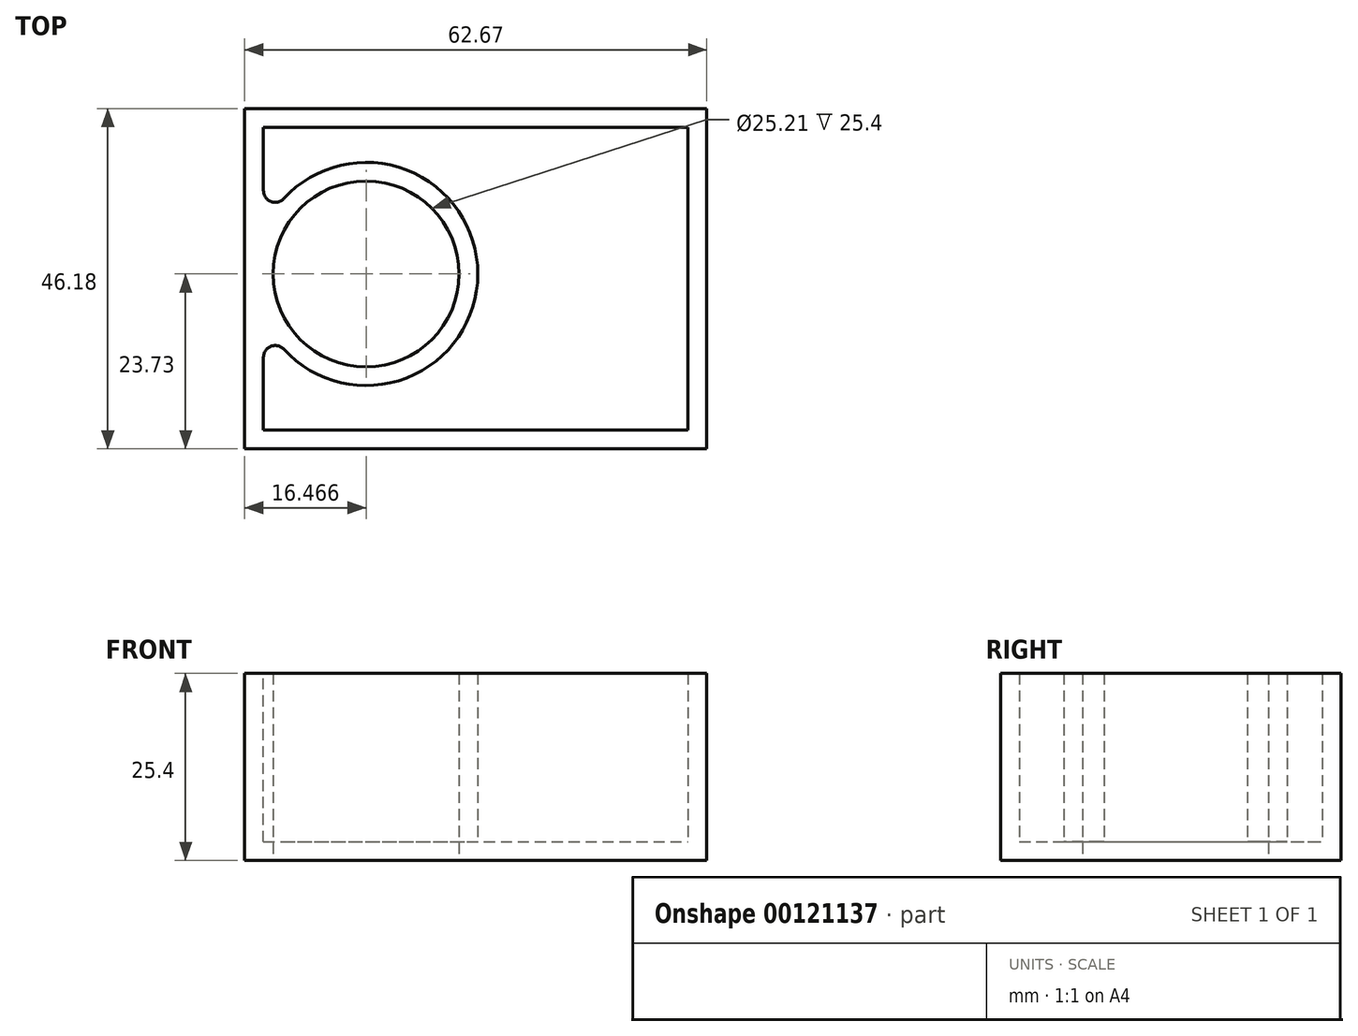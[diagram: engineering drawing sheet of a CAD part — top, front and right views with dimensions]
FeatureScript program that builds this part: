
annotation { "Feature Type Name" : "Feature", "Feature Type Description" : "" }
export const myFeature = defineFeature(function(context is Context, id is Id, definition is map)
    precondition{}
    {
        {
            var Q0;
            Q0=qCreatedBy(makeId("Top.planeOp"),FACE);
            var sketch = newSketch(context, id + "F0", { "sketchPlane" : qUnion([Q0])});
            skLineSegment(sketch, "E0.bottom", {"start": v(0, 0) * mm, "end": v(62.67, 0) * mm});
            skLineSegment(sketch, "E0.top", {"start": v(0, 46.18) * mm, "end": v(62.67, 46.18) * mm});
            skLineSegment(sketch, "E0.left", {"start": v(0, 0) * mm, "end": v(0, 46.18) * mm});
            skLineSegment(sketch, "E0.right", {"start": v(62.67, 0) * mm, "end": v(62.67, 46.18) * mm});
            skCircle(sketch, "E1", {"center": v(16.47, 23.73) * mm, "radius": 12.6 * mm});
            skSolve(sketch);
        }
        {
            var Q0;
            Q0 = qSketchRegion(id + "F0", true);
            extrude(context, id + "F1", {"entities" : qUnion([Q0]), "depth" : 25.4 * mm});
        }
        {
            var Q0;
            Q0=makeQuery(id+"F1.opExtrude","CAP_FACE",FACE,{"disambiguationData":[OSD([sQuery(id+"F0.wireOp",EDGE,"E0.bottom"),sQuery(id+"F0.wireOp",EDGE,"E0.top"),sQuery(id+"F0.wireOp",EDGE,"E0.left"),sQuery(id+"F0.wireOp",EDGE,"E0.right"),sQuery(id+"F0.wireOp",EDGE,"E1")])],"isStart":false});
            shell(context, id + "F2", {"entities" : qUnion([Q0]), "thickness" : 2.54 * mm});
        }
        {
            var Q0;
            Q0=makeQuery(id+"F2.opShell","TWEAK_EDGE",EDGE,{"disambiguationData":[OD(0.0)],"derivedFrom":[makeQuery(id+"F1.opExtrude","SWEPT_FACE",FACE,{"disambiguationData":[OSD([sQuery(id+"F0.wireOp",EDGE,"E0.left")])]}),makeQuery(id+"F1.opExtrude","SWEPT_FACE",FACE,{"disambiguationData":[OSD([sQuery(id+"F0.wireOp",EDGE,"E1")])]})]});
            var Q1;
            Q1=makeQuery(id+"F2.opShell","TWEAK_EDGE",EDGE,{"disambiguationData":[OD(1.0)],"derivedFrom":[makeQuery(id+"F1.opExtrude","SWEPT_FACE",FACE,{"disambiguationData":[OSD([sQuery(id+"F0.wireOp",EDGE,"E0.left")])]}),makeQuery(id+"F1.opExtrude","SWEPT_FACE",FACE,{"disambiguationData":[OSD([sQuery(id+"F0.wireOp",EDGE,"E1")])]})]});
            fillet(context, id + "F3", {"entities" : qUnion([Q0, Q1]), "radius" : 1.59 * mm, "tangentPropagation" : true, "allowEdgeOverflow" : false});
        }
    });
